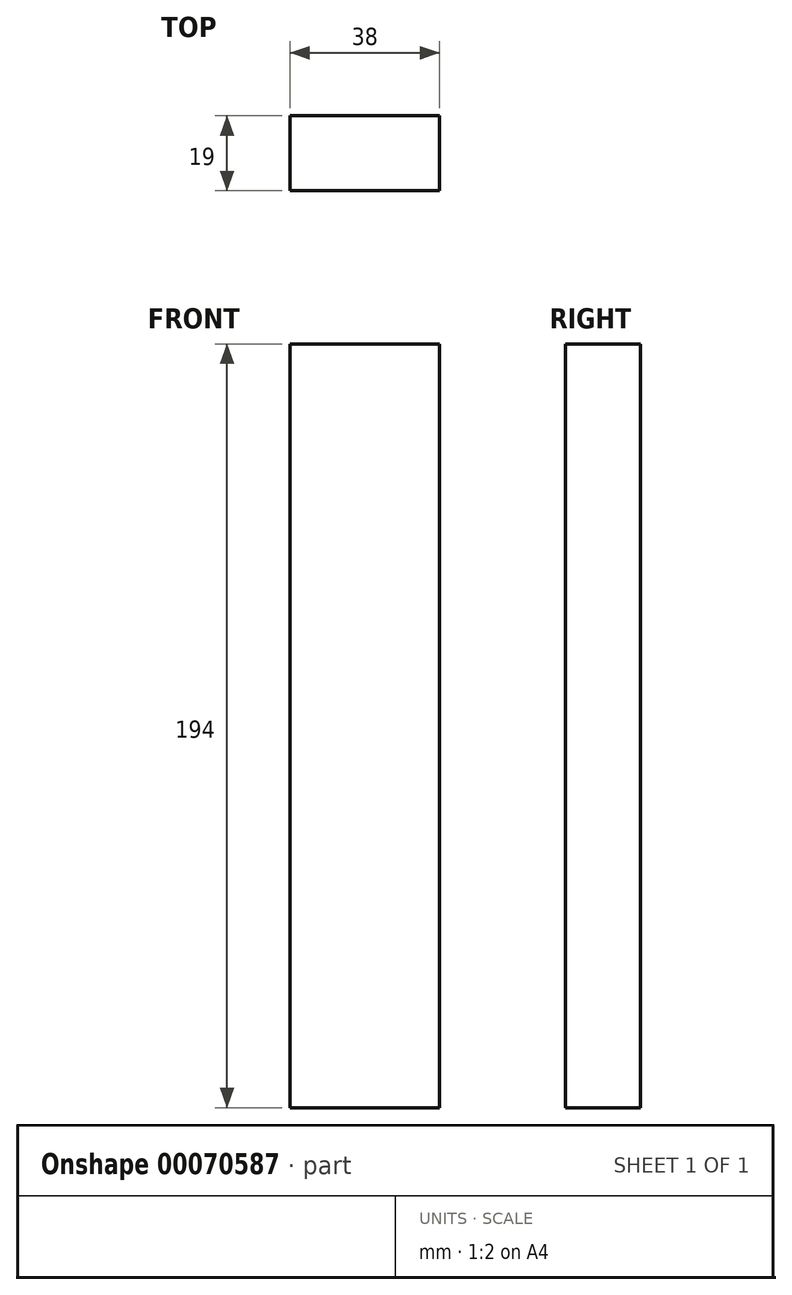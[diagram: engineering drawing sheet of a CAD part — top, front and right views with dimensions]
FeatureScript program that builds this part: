
annotation { "Feature Type Name" : "Feature", "Feature Type Description" : "" }
export const myFeature = defineFeature(function(context is Context, id is Id, definition is map)
    precondition{}
    {
        {
            var Q0;
            Q0=qCreatedBy(makeId("Front.planeOp"),FACE);
            var sketch = newSketch(context, id + "F0", { "sketchPlane" : qUnion([Q0])});
            skLineSegment(sketch, "E0.bottom", {"start": v(0, 0) * mm, "end": v(38, 0) * mm});
            skLineSegment(sketch, "E0.top", {"start": v(0, -194) * mm, "end": v(38, -194) * mm});
            skLineSegment(sketch, "E0.left", {"start": v(0, 0) * mm, "end": v(0, -194) * mm});
            skLineSegment(sketch, "E0.right", {"start": v(38, 0) * mm, "end": v(38, -194) * mm});
            skSolve(sketch);
        }
        {
            var Q0;
            Q0 = qSketchRegion(id + "F0", true);
            extrude(context, id + "F1", {"entities" : qUnion([Q0]), "depth" : 19 * mm});
        }
    });
